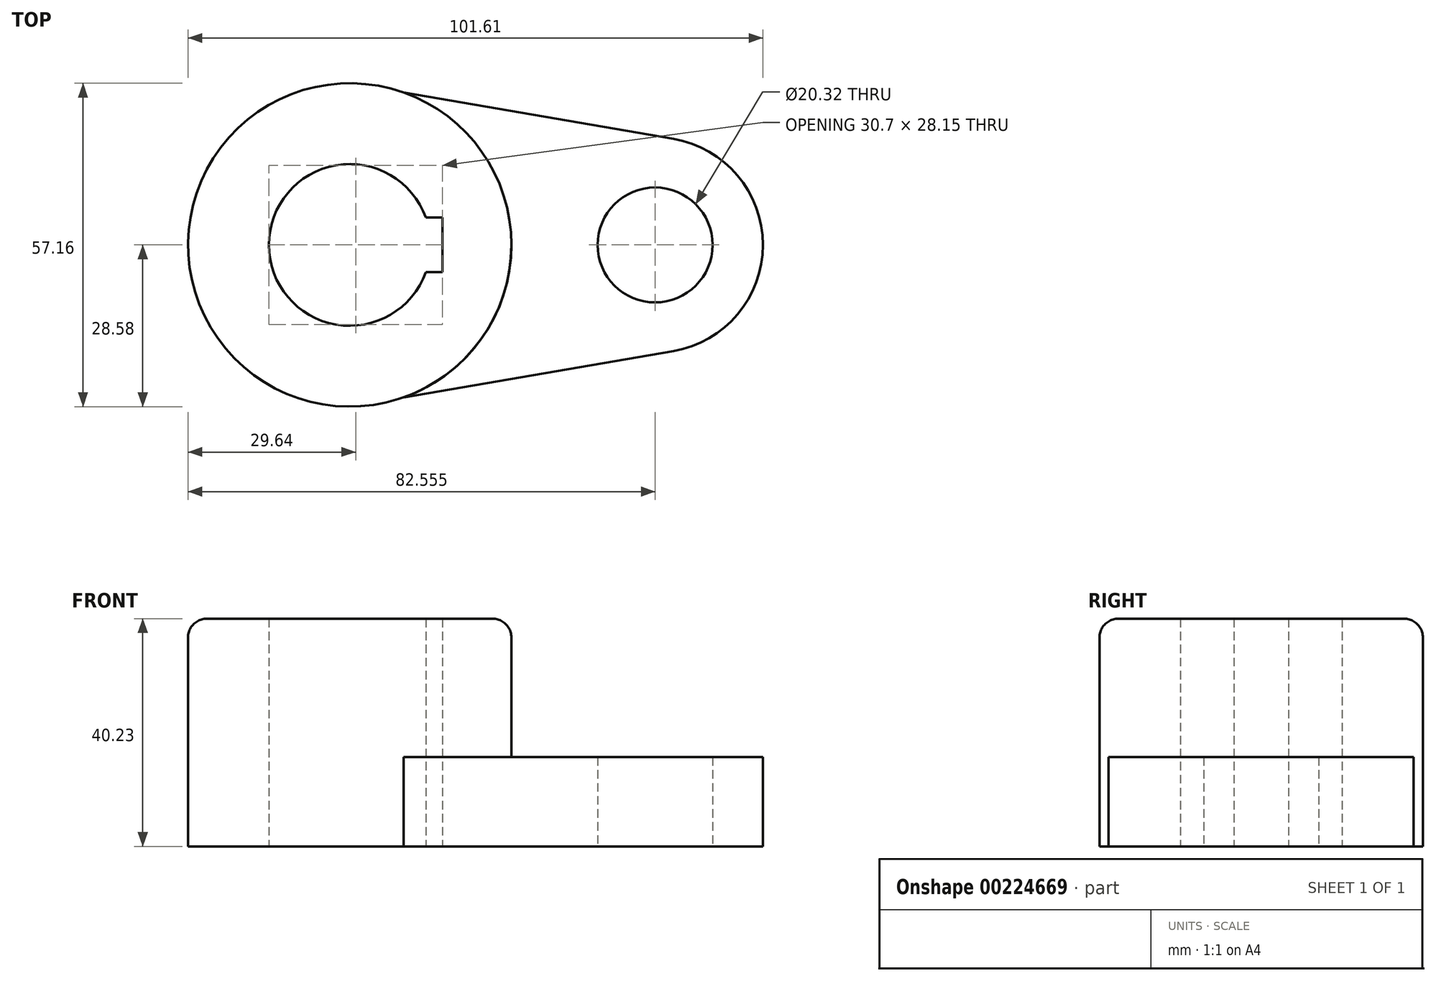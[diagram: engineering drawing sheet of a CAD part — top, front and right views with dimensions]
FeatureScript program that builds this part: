
annotation { "Feature Type Name" : "Feature", "Feature Type Description" : "" }
export const myFeature = defineFeature(function(context is Context, id is Id, definition is map)
    precondition{}
    {
        {
            var Q0;
            Q0=qCreatedBy(makeId("Top.planeOp"),FACE);
            var sketch = newSketch(context, id + "F0", { "sketchPlane" : qUnion([Q0])});
            skCircle(sketch, "E0", {"center": v(0, 0) * mm, "radius": 28.58 * mm});
            skArc(sketch, "E1", {"start": v(13.45, 4.83) * mm, "mid": v(-14.29, 0) * mm, "end": v(13.45, -4.83) * mm});
            skCircle(sketch, "E2", {"center": v(53.98, 0) * mm, "radius": 10.16 * mm});
            skPoint(sketch, "E3.orphan", {"position": v(0, 28.58) * mm});
            skPoint(sketch, "E4.orphan", {"position": v(0, -28.58) * mm});
            skLineSegment(sketch, "E5.bottom", {"start": v(16.4, 4.83) * mm, "end": v(13.45, 4.83) * mm});
            skLineSegment(sketch, "E5.top", {"start": v(16.4, -4.83) * mm, "end": v(13.45, -4.83) * mm});
            skLineSegment(sketch, "E5.left", {"start": v(16.4, 4.83) * mm, "end": v(16.4, -4.83) * mm});
            skPoint(sketch, "E6.orphan", {"position": v(-16.4, 4.83) * mm});
            skPoint(sketch, "E7.orphan", {"position": v(-16.4, -4.83) * mm});
            skLineSegment(sketch, "E8", {"start": v(9.51, 26.95) * mm, "end": v(57.2, 18.78) * mm});
            skLineSegment(sketch, "E9", {"start": v(9.51, -26.95) * mm, "end": v(57.2, -18.78) * mm});
            skArc(sketch, "E10", {"start": v(57.2, 18.78) * mm, "mid": v(73.03, 0) * mm, "end": v(57.2, -18.78) * mm});
            skSolve(sketch);
        }
        {
            var Q0;
            Q0=makeQuery(id+"F0.imprint","IMPRINT",FACE,{"disambiguationData":[TD([[makeQuery(id+"F0.imprint","IMPRINT",EDGE,{"derivedFrom":sQuery(id+"F0.wireOp",EDGE,"E2")}),-1.0]])]});
            extrude(context, id + "F1", {"entities" : qUnion([Q0]), "depth" : 15.77 * mm});
        }
        {
            var Q0;
            Q0=makeQuery(id+"F0.imprint","IMPRINT",FACE,{"disambiguationData":[TD([[makeQuery(id+"F0.imprint","IMPRINT",EDGE,{"derivedFrom":sQuery(id+"F0.wireOp",EDGE,"E1")}),-1.0]])]});
            extrude(context, id + "F2", {"entities" : qUnion([Q0]), "operationType" : NewBodyOperationType.ADD, "depth" : 40.23 * mm});
        }
        {
            var Q0;
            Q0=makeQuery(id+"F2.opExtrude","CAP_EDGE",EDGE,{"disambiguationData":[OSD([sQuery(id+"F0.wireOp",EDGE,"E0")])],"isStart":false});
            fillet(context, id + "F3", {"entities" : qUnion([Q0]), "radius" : 3.3 * mm, "tangentPropagation" : true, "allowEdgeOverflow" : false});
        }
    });
